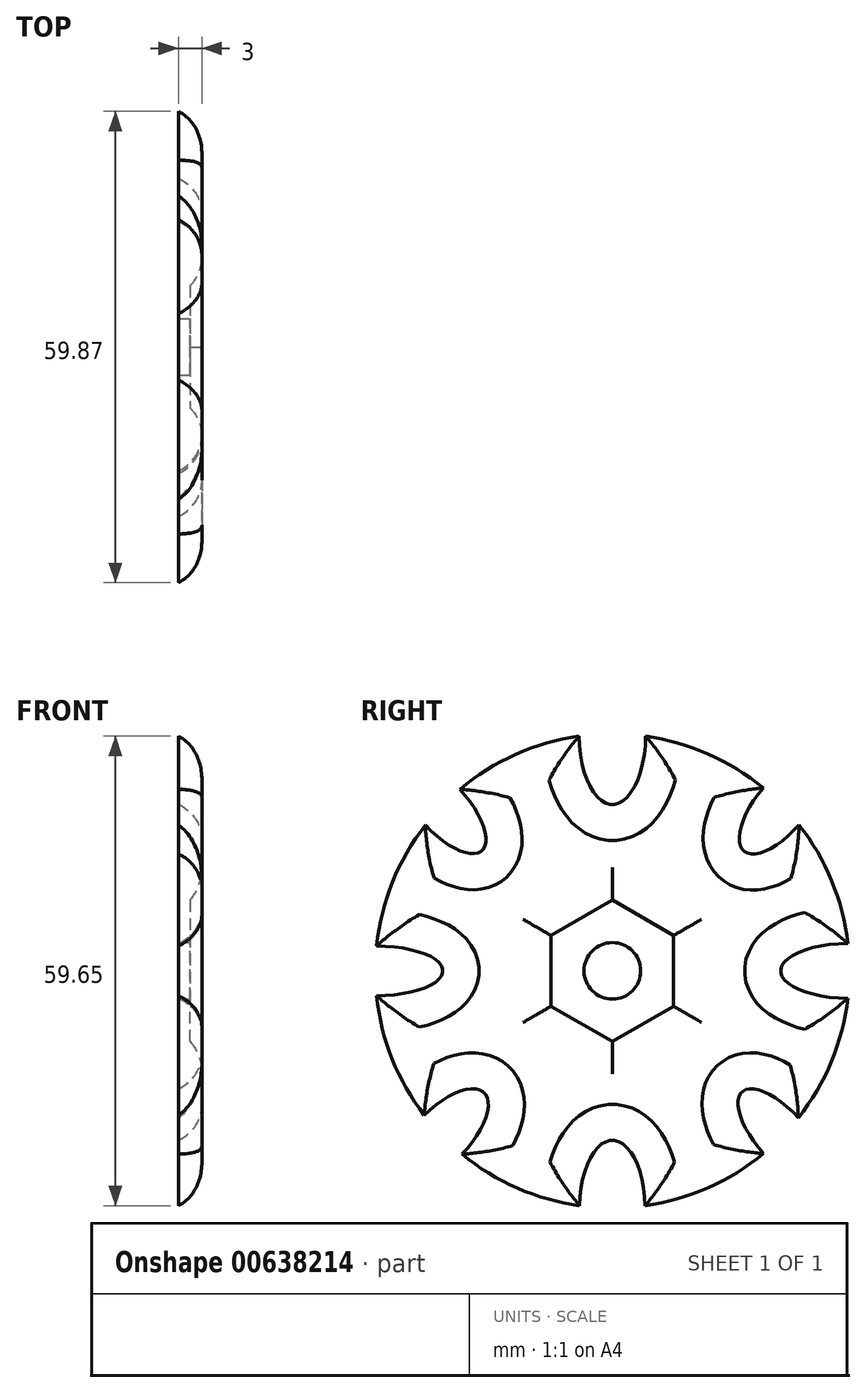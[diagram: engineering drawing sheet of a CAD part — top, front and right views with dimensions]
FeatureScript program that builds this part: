
annotation { "Feature Type Name" : "Feature", "Feature Type Description" : "" }
export const myFeature = defineFeature(function(context is Context, id is Id, definition is map)
    precondition{}
    {
        {
            var Q0;
            Q0=qCreatedBy(makeId("Right.planeOp"),FACE);
            var sketch = newSketch(context, id + "F0", { "sketchPlane" : qUnion([Q0])});
            skCircle(sketch, "E0", {"center": v(0, 0) * mm, "radius": 30.12 * mm});
            skSolve(sketch);
        }
        {
            var Q0;
            Q0=makeQuery(id+"F0.imprint","IMPRINT",FACE,{"disambiguationData":[TD([[makeQuery(id+"F0.imprint","IMPRINT",EDGE,{"derivedFrom":sQuery(id+"F0.wireOp",EDGE,"E0")}),1.0]])]});
            extrude(context, id + "F1", {"entities" : qUnion([Q0]), "depth" : 3 * mm, "offsetDistance" : 25 * mm});
        }
        {
            var Q0;
            Q0=makeQuery(id+"F1.opExtrude","CAP_FACE",FACE,{"disambiguationData":[OSD([sQuery(id+"F0.wireOp",EDGE,"E0")])],"isStart":false});
            var sketch = newSketch(context, id + "F2", { "sketchPlane" : qUnion([Q0])});
            skEllipse(sketch, "E1", {"center": v(0, 30.12) * mm, "majorRadius": 8.97 * mm, "minorRadius": 4.24 * mm, "majorAxis": v(0, -1)});
            skEllipse(sketch, "E2", {"center": v(30.12, 0) * mm, "majorRadius": 8.72 * mm, "minorRadius": 3.5 * mm, "majorAxis": v(-1, 0)});
            skEllipse(sketch, "E3", {"center": v(0, -30.12) * mm, "majorRadius": 8.59 * mm, "minorRadius": 4.15 * mm, "majorAxis": v(0, -1)});
            skEllipse(sketch, "E4", {"center": v(-30.12, 0) * mm, "majorRadius": 8.6 * mm, "minorRadius": 3.17 * mm, "majorAxis": v(-1, 0)});
            skSolve(sketch);
        }
        {
            var Q0;
            {var subQ0=sQuery(id+"F2.wireOp",EDGE,"E4");var subQ1=makeQuery(id+"F1.opExtrude","CAP_EDGE",EDGE,{"disambiguationData":[OSD([sQuery(id+"F0.wireOp",EDGE,"E0")])],"isStart":false});var subQ2=makeQuery(id+"F2.imprint","INTERSECT",VERTEX,{"disambiguationData":[OD(0.0)],"derivedFrom":[subQ1,subQ0]});Q0=makeQuery(id+"F2.imprint","IMPRINT",FACE,{"disambiguationData":[TD([[makeQuery(id+"F2.imprint","IMPRINT",EDGE,{"disambiguationData":[TD([[subQ2,-1.0]])],"derivedFrom":subQ0}),1.0]])]});}
            var Q1;
            {var subQ0=sQuery(id+"F2.wireOp",EDGE,"E2");var subQ1=makeQuery(id+"F1.opExtrude","CAP_EDGE",EDGE,{"disambiguationData":[OSD([sQuery(id+"F0.wireOp",EDGE,"E0")])],"isStart":false});var subQ2=makeQuery(id+"F2.imprint","INTERSECT",VERTEX,{"disambiguationData":[OD(0.0)],"derivedFrom":[subQ1,subQ0]});Q1=makeQuery(id+"F2.imprint","IMPRINT",FACE,{"disambiguationData":[TD([[makeQuery(id+"F2.imprint","IMPRINT",EDGE,{"disambiguationData":[TD([[subQ2,1.0]])],"derivedFrom":subQ0}),1.0]])]});}
            var Q2;
            {var subQ0=sQuery(id+"F2.wireOp",EDGE,"E3");var subQ1=makeQuery(id+"F1.opExtrude","CAP_EDGE",EDGE,{"disambiguationData":[OSD([sQuery(id+"F0.wireOp",EDGE,"E0")])],"isStart":false});var subQ2=makeQuery(id+"F2.imprint","INTERSECT",VERTEX,{"disambiguationData":[OD(0.0)],"derivedFrom":[subQ1,subQ0]});Q2=makeQuery(id+"F2.imprint","IMPRINT",FACE,{"disambiguationData":[TD([[makeQuery(id+"F2.imprint","IMPRINT",EDGE,{"disambiguationData":[TD([[subQ2,1.0]])],"derivedFrom":subQ0}),1.0]])]});}
            var Q3;
            {var subQ0=sQuery(id+"F2.wireOp",EDGE,"E1");var subQ1=makeQuery(id+"F1.opExtrude","CAP_EDGE",EDGE,{"disambiguationData":[OSD([sQuery(id+"F0.wireOp",EDGE,"E0")])],"isStart":false});var subQ2=makeQuery(id+"F2.imprint","INTERSECT",VERTEX,{"disambiguationData":[OD(0.0)],"derivedFrom":[subQ1,subQ0]});Q3=makeQuery(id+"F2.imprint","IMPRINT",FACE,{"disambiguationData":[TD([[makeQuery(id+"F2.imprint","IMPRINT",EDGE,{"disambiguationData":[TD([[subQ2,-1.0]])],"derivedFrom":subQ0}),1.0]])]});}
            extrude(context, id + "F3", {"entities" : qUnion([Q0, Q1, Q2, Q3]), "operationType" : NewBodyOperationType.REMOVE, "oppositeDirection" : true, "depth" : 3 * mm, "offsetDistance" : 25 * mm});
        }
        {
            var Q0;
            Q0=makeQuery(id+"F1.opExtrude","CAP_FACE",FACE,{"disambiguationData":[OSD([sQuery(id+"F0.wireOp",EDGE,"E0")])],"isStart":false});
            var sketch = newSketch(context, id + "F4", { "sketchPlane" : qUnion([Q0])});
            skCircle(sketch, "E5.cCircle", {"center": v(0, 0) * mm, "radius": 8.99 * mm, "construction": true});
            skLineSegment(sketch, "E5.0", {"start": v(0, -8.99) * mm, "end": v(-7.78, -4.5) * mm});
            skLineSegment(sketch, "E5.1", {"start": v(-7.78, -4.5) * mm, "end": v(-7.78, 4.5) * mm});
            skLineSegment(sketch, "E5.2", {"start": v(-7.78, 4.5) * mm, "end": v(0, 8.99) * mm});
            skLineSegment(sketch, "E5.3", {"start": v(0, 8.99) * mm, "end": v(7.78, 4.5) * mm});
            skLineSegment(sketch, "E5.4", {"start": v(7.78, 4.5) * mm, "end": v(7.78, -4.5) * mm});
            skLineSegment(sketch, "E5.5", {"start": v(7.78, -4.5) * mm, "end": v(0, -8.99) * mm});
            skSolve(sketch);
        }
        {
            var Q0;
            Q0=makeQuery(id+"F4.imprint","IMPRINT",FACE,{"disambiguationData":[TD([[makeQuery(id+"F4.imprint","IMPRINT",EDGE,{"derivedFrom":sQuery(id+"F4.wireOp",EDGE,"E5.0")}),-1.0]])]});
            extrude(context, id + "F5", {"entities" : qUnion([Q0]), "operationType" : NewBodyOperationType.REMOVE, "oppositeDirection" : true, "depth" : 1.5 * mm, "offsetDistance" : 25 * mm});
        }
        {
            var Q0;
            Q0=makeQuery(id+"F1.opExtrude","CAP_FACE",FACE,{"disambiguationData":[OSD([sQuery(id+"F0.wireOp",EDGE,"E0")])],"isStart":false});
            var sketch = newSketch(context, id + "F6", { "sketchPlane" : qUnion([Q0])});
            skEllipse(sketch, "E6", {"center": v(21.56, 21.03) * mm, "majorRadius": 7.57 * mm, "minorRadius": 3.25 * mm, "majorAxis": v(-0.64, -0.77)});
            skEllipse(sketch, "E7", {"center": v(-21.68, 20.91) * mm, "majorRadius": 7.62 * mm, "minorRadius": 3.16 * mm, "majorAxis": v(0.67, -0.74)});
            skEllipse(sketch, "E8", {"center": v(21.53, -21.06) * mm, "majorRadius": 7.6 * mm, "minorRadius": 3.17 * mm, "majorAxis": v(-0.66, 0.75)});
            skEllipse(sketch, "E9", {"center": v(-21.65, -20.94) * mm, "majorRadius": 7.63 * mm, "minorRadius": 3.44 * mm, "majorAxis": v(0.7, 0.71)});
            skSolve(sketch);
        }
        {
            var Q0;
            Q0 = qSketchRegion(id + "F6", true);
            extrude(context, id + "F7", {"entities" : qUnion([Q0]), "operationType" : NewBodyOperationType.REMOVE, "oppositeDirection" : true, "depth" : 3 * mm, "offsetDistance" : 25 * mm});
        }
        {
            var Q0;
            Q0=makeQuery(id+"F1.opExtrude","CAP_FACE",FACE,{"disambiguationData":[OSD([sQuery(id+"F0.wireOp",EDGE,"E0")])],"isStart":false});
            fillet(context, id + "F8", {"entities" : qUnion([Q0]), "radius" : 5 * mm, "tangentPropagation" : true, "allowEdgeOverflow" : false});
        }
        {
            var Q0;
            Q0=makeQuery(id+"F1.opExtrude","CAP_FACE",FACE,{"disambiguationData":[OSD([sQuery(id+"F0.wireOp",EDGE,"E0")])],"isStart":false});
            var sketch = newSketch(context, id + "F9", { "sketchPlane" : qUnion([Q0])});
            skCircle(sketch, "E10", {"center": v(0, 0) * mm, "radius": 3.6 * mm});
            skSolve(sketch);
        }
        {
            var Q0;
            Q0=makeQuery(id+"F9.imprint","IMPRINT",FACE,{"disambiguationData":[TD([[makeQuery(id+"F9.imprint","IMPRINT",EDGE,{"derivedFrom":sQuery(id+"F9.wireOp",EDGE,"E10")}),1.0]])]});
            extrude(context, id + "F10", {"entities" : qUnion([Q0]), "operationType" : NewBodyOperationType.REMOVE, "oppositeDirection" : true, "depth" : 3 * mm, "offsetDistance" : 25 * mm});
        }
    });
